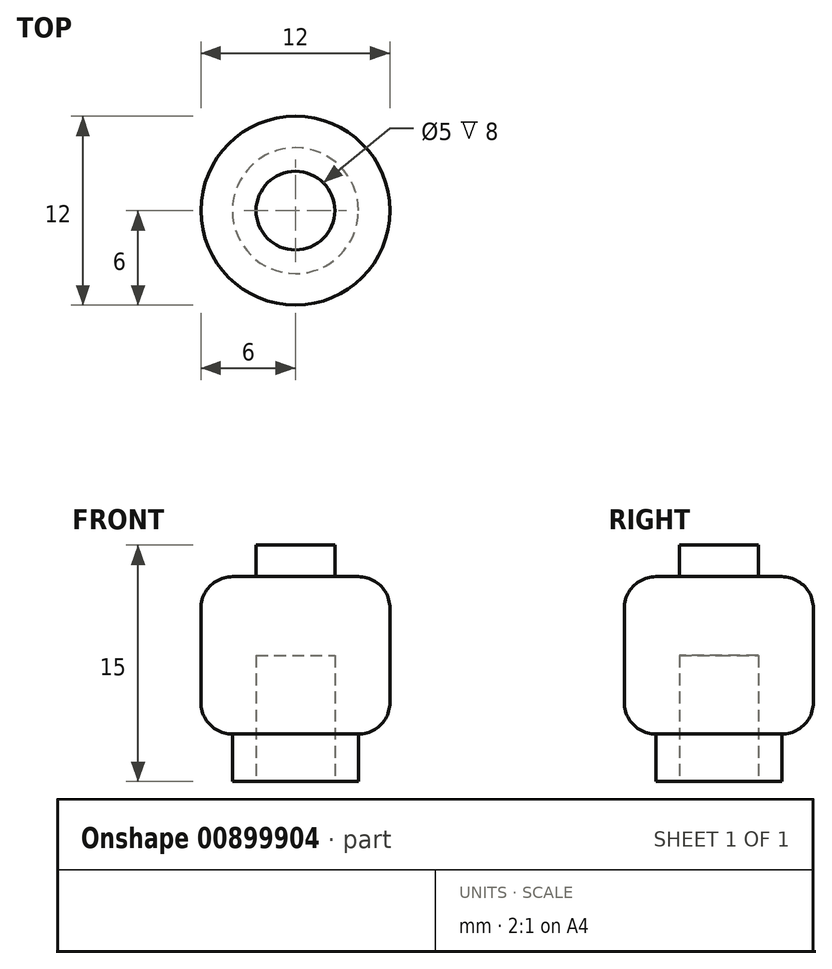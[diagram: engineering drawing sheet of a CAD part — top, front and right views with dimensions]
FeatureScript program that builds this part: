
annotation { "Feature Type Name" : "Feature", "Feature Type Description" : "" }
export const myFeature = defineFeature(function(context is Context, id is Id, definition is map)
    precondition{}
    {
        {
            var Q0;
            Q0=qCreatedBy(makeId("Top.planeOp"),FACE);
            var sketch = newSketch(context, id + "F0", { "sketchPlane" : qUnion([Q0])});
            skCircle(sketch, "E0", {"center": v(0, 0) * mm, "radius": 4 * mm});
            skSolve(sketch);
        }
        {
            var Q0;
            Q0=makeQuery(id+"F0.imprint","IMPRINT",FACE,{"disambiguationData":[TD([[makeQuery(id+"F0.imprint","IMPRINT",EDGE,{"derivedFrom":sQuery(id+"F0.wireOp",EDGE,"E0")}),1.0]])]});
            extrude(context, id + "F1", {"entities" : qUnion([Q0]), "depth" : 3 * mm, "offsetDistance" : 25.4 * mm});
        }
        {
            var Q0;
            Q0=makeQuery(id+"F1.opExtrude","CAP_FACE",FACE,{"disambiguationData":[OSD([sQuery(id+"F0.wireOp",EDGE,"E0")])],"isStart":false});
            var sketch = newSketch(context, id + "F2", { "sketchPlane" : qUnion([Q0])});
            skCircle(sketch, "E1", {"center": v(0, 0) * mm, "radius": 6 * mm});
            skSolve(sketch);
        }
        {
            var Q0;
            Q0 = qSketchRegion(id + "F2", true);
            extrude(context, id + "F3", {"entities" : qUnion([Q0]), "operationType" : NewBodyOperationType.ADD, "depth" : 10 * mm, "offsetDistance" : 25.4 * mm});
        }
        {
            var Q0;
            Q0=makeQuery(id+"F3.opExtrude","CAP_FACE",FACE,{"disambiguationData":[OSD([sQuery(id+"F2.wireOp",EDGE,"E1")])],"isStart":false});
            var sketch = newSketch(context, id + "F4", { "sketchPlane" : qUnion([Q0])});
            skCircle(sketch, "E2", {"center": v(0, 0) * mm, "radius": 2.5 * mm});
            skSolve(sketch);
        }
        {
            var Q0;
            Q0 = qSketchRegion(id + "F4", true);
            extrude(context, id + "F5", {"entities" : qUnion([Q0]), "operationType" : NewBodyOperationType.ADD, "depth" : 2 * mm, "offsetDistance" : 25.4 * mm});
        }
        {
            var Q0;
            Q0=makeQuery(id+"F3.opExtrude","CAP_EDGE",EDGE,{"disambiguationData":[OSD([sQuery(id+"F2.wireOp",EDGE,"E1")])],"isStart":false});
            var Q1;
            Q1=makeQuery(id+"F3.opExtrude","CAP_EDGE",EDGE,{"disambiguationData":[OSD([sQuery(id+"F2.wireOp",EDGE,"E1")])],"isStart":true});
            fillet(context, id + "F6", {"entities" : qUnion([Q0, Q1]), "radius" : 2 * mm, "tangentPropagation" : true, "allowEdgeOverflow" : false});
        }
        {
            var Q0;
            Q0=makeQuery(id+"F1.opExtrude","CAP_FACE",FACE,{"disambiguationData":[OSD([sQuery(id+"F0.wireOp",EDGE,"E0")])],"isStart":true});
            var sketch = newSketch(context, id + "F7", { "sketchPlane" : qUnion([Q0])});
            skCircle(sketch, "E3", {"center": v(0, 0) * mm, "radius": 2.5 * mm});
            skSolve(sketch);
        }
        {
            var Q0;
            Q0 = qSketchRegion(id + "F7", true);
            extrude(context, id + "F8", {"entities" : qUnion([Q0]), "operationType" : NewBodyOperationType.REMOVE, "oppositeDirection" : true, "depth" : 8 * mm, "offsetDistance" : 25.4 * mm});
        }
    });
